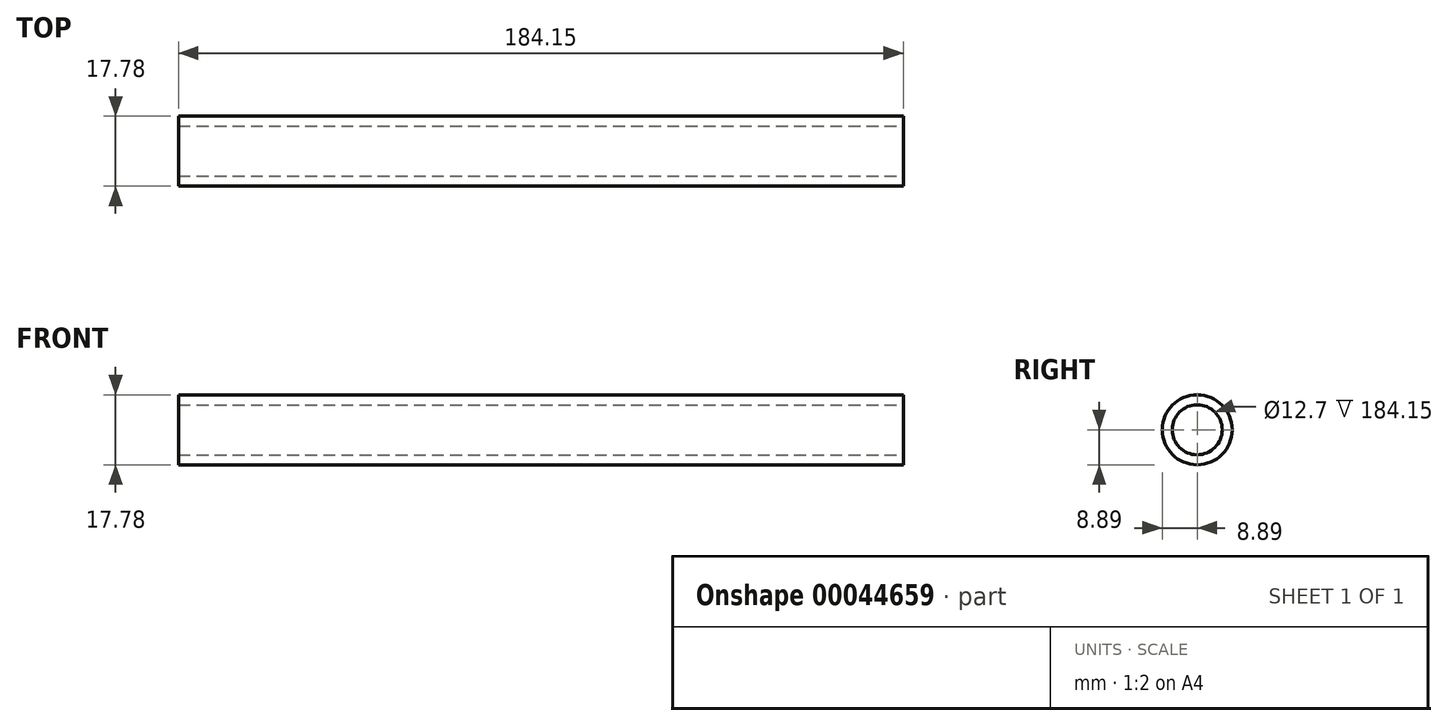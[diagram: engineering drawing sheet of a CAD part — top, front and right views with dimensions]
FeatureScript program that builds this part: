
annotation { "Feature Type Name" : "Feature", "Feature Type Description" : "" }
export const myFeature = defineFeature(function(context is Context, id is Id, definition is map)
    precondition{}
    {
        {
            var Q0;
            Q0=qCreatedBy(makeId("Right.planeOp"),FACE);
            var sketch = newSketch(context, id + "F0", { "sketchPlane" : qUnion([Q0])});
            skCircle(sketch, "E0", {"center": v(0, 0) * mm, "radius": 8.9 * mm});
            skSolve(sketch);
        }
        {
            var Q0;
            Q0=makeQuery(id+"F0.imprint","IMPRINT",FACE,{"disambiguationData":[TD([[makeQuery(id+"F0.imprint","IMPRINT",EDGE,{"derivedFrom":sQuery(id+"F0.wireOp",EDGE,"E0")}),1.0]])]});
            extrude(context, id + "F1", {"entities" : qUnion([Q0]), "oppositeDirection" : true, "depth" : 184.15 * mm});
        }
        {
            var Q0;
            Q0=makeQuery(id+"F1.opExtrude","CAP_FACE",FACE,{"disambiguationData":[OSD([sQuery(id+"F0.wireOp",EDGE,"E0")])],"isStart":true});
            var sketch = newSketch(context, id + "F2", { "sketchPlane" : qUnion([Q0])});
            skPoint(sketch, "E1", {"position": v(0, 0) * mm});
            skSolve(sketch);
        }
        {
            var Q0;
            Q0=sQuery(id+"F2.wireOp",VERTEX,"E1");
            var Q1;
            Q1=makeQuery(id+"F1.opExtrude","SWEPT_BODY",BODY,{"disambiguationData":[OSD([sQuery(id+"F0.wireOp",EDGE,"E0")])]});
            hole(context, id + "F3", {"style" : HoleStyle.SIMPLE, "holeDiameter" : 12.7 * mm, "endStyle" : HoleEndStyle.THROUGH, "locations" : qUnion([Q0]), "scope" : qUnion([Q1])});
        }
    });
